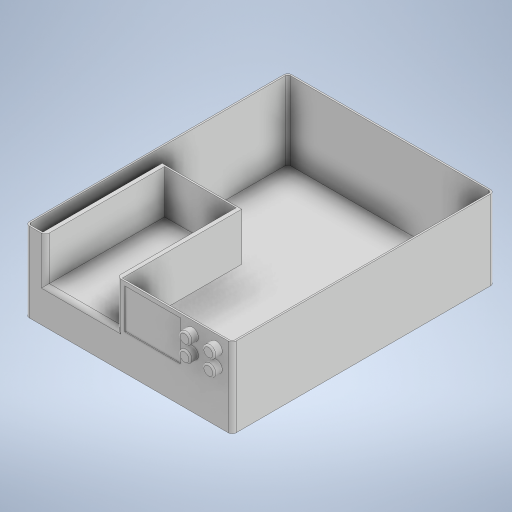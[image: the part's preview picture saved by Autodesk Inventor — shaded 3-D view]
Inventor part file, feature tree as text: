
AUTODESK INVENTOR PART (.ipt)
format: ipt  version: 2023 (Build 270158000, 158)  size: 325,632 bytes
history: native  units: mm
features: extrude x5, sketch x5, fillet x3, projected_geometry x3, shell x1
ambient origin geometry x8: Origin, YZ Plane, XZ Plane, XY Plane, X Axis, Y Axis, Z Axis, Center Point
bodies: Solid1 (feature_tree)
feature tree (17):
  extrude  "Extrusion1"  Depth=330.0mm
  fillet  "Fillet1"  Radius=100.0mm
  shell  "Shell1"  Thickness=2.0mm
  extrude  "Extrusion3"  Depth=100.0mm
  extrude  "Extrusion4"  Depth=150.0mm
  fillet  "Fillet3"  Radius=150.0mm
  extrude  "Extrusion5"  Depth=5.0mm
  fillet  "Fillet4"  Radius=5.0mm
  extrude  "Extrusion6"  Depth=5.0mm
  sketch  "Sketch1"  dims[d0=260.0mm d1=330.0mm d2=100.0mm d3=0.0mm d10=2.0mm]
  sketch  "Sketch3"  dims[d11=5.0mm d13=100.0mm]
  sketch  "Sketch4"  dims[d14=60.0mm d15=15.0mm d16=150.0mm d17=0.0mm]
  projected_geometry  "Projected Loop1"
  projected_geometry  "Projected Loop2"
  projected_geometry  "Projected Loop3"
  sketch  "Sketch5"  dims[d18=5.0mm d19=5.0mm d20=5.0mm]
  sketch  "Sketch6"  dims[d21=150.0mm d22=0.0mm d23=5.0mm d24=15.0mm d25=15.0mm d26=15.0mm d27=20.0mm d29=30.0mm d30=20.0mm d32=20.0mm d35=10.0mm d36=0.0mm d37=2.0mm d38=5.0mm d39=5.0mm d40=70.0mm d41=50.0mm d42=1.0mm d43=0.0mm d44=0.5mm d45=0.872665mm d46=0.5mm d47=0.872665mm]
